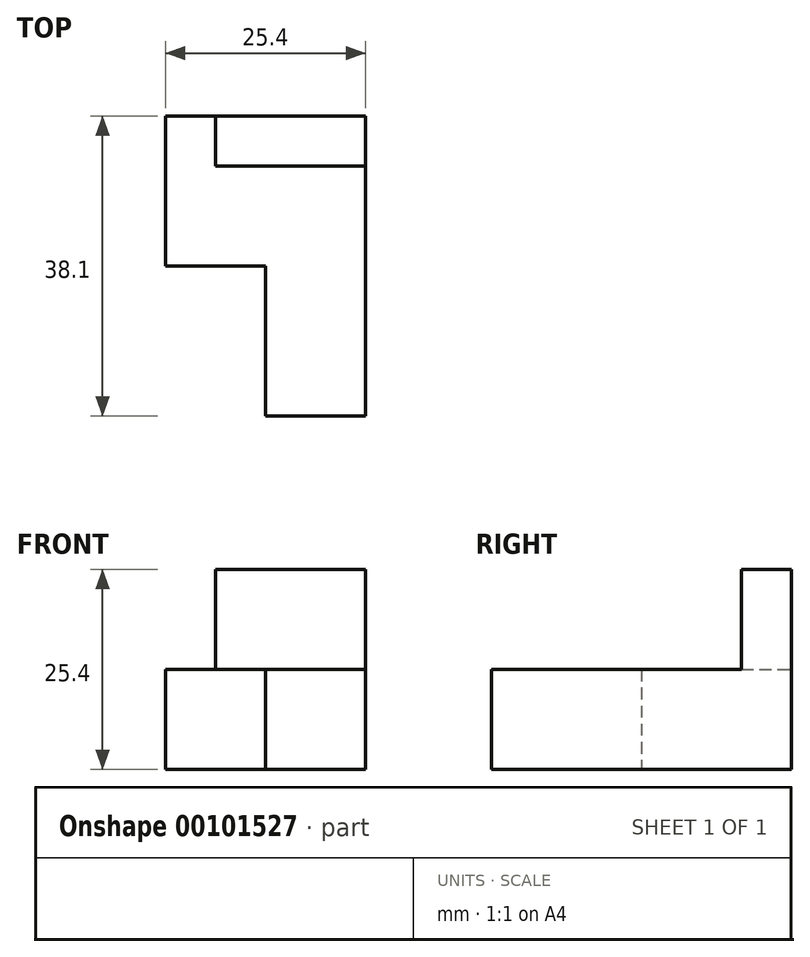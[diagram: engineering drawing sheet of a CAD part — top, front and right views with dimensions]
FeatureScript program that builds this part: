
annotation { "Feature Type Name" : "Feature", "Feature Type Description" : "" }
export const myFeature = defineFeature(function(context is Context, id is Id, definition is map)
    precondition{}
    {
        {
            var Q0;
            Q0=qCreatedBy(makeId("Front.planeOp"),FACE);
            var sketch = newSketch(context, id + "F0", { "sketchPlane" : qUnion([Q0])});
            skLineSegment(sketch, "E0", {"start": v(0, 0) * mm, "end": v(0, 12.7) * mm});
            skLineSegment(sketch, "E1", {"start": v(0, 12.7) * mm, "end": v(12.7, 12.7) * mm});
            skLineSegment(sketch, "E2", {"start": v(12.7, 12.7) * mm, "end": v(12.7, 0) * mm});
            skLineSegment(sketch, "E3", {"start": v(12.7, 0) * mm, "end": v(0, 0) * mm});
            skLineSegment(sketch, "E4", {"start": v(12.7, 12.7) * mm, "end": v(25.4, 12.7) * mm});
            skLineSegment(sketch, "E5", {"start": v(25.4, 12.7) * mm, "end": v(25.4, 0) * mm});
            skLineSegment(sketch, "E6", {"start": v(25.4, 0) * mm, "end": v(12.7, 0) * mm});
            skSolve(sketch);
        }
        {
            var Q0;
            Q0=makeQuery(id+"F0.imprint","IMPRINT",FACE,{"disambiguationData":[TD([[makeQuery(id+"F0.imprint","IMPRINT",EDGE,{"derivedFrom":sQuery(id+"F0.wireOp",EDGE,"E2")}),1.0]])]});
            extrude(context, id + "F1", {"entities" : qUnion([Q0]), "depth" : 38.1 * mm});
        }
        {
            var Q0;
            Q0=makeQuery(id+"F0.imprint","IMPRINT",FACE,{"disambiguationData":[TD([[makeQuery(id+"F0.imprint","IMPRINT",EDGE,{"derivedFrom":sQuery(id+"F0.wireOp",EDGE,"E0")}),-1.0]])]});
            extrude(context, id + "F2", {"entities" : qUnion([Q0]), "operationType" : NewBodyOperationType.ADD, "depth" : 19.05 * mm});
        }
        {
            var Q0;
            Q0=makeQuery(id+"F1.opExtrude","SWEPT_FACE",FACE,{"disambiguationData":[OSD([sQuery(id+"F0.wireOp",EDGE,"E5")])]});
            var sketch = newSketch(context, id + "F3", { "sketchPlane" : qUnion([Q0])});
            skLineSegment(sketch, "E7", {"start": v(0, 12.7) * mm, "end": v(0, 25.4) * mm});
            skLineSegment(sketch, "E8", {"start": v(0, 25.4) * mm, "end": v(-6.35, 25.4) * mm});
            skLineSegment(sketch, "E9", {"start": v(-6.35, 25.4) * mm, "end": v(-6.35, 12.7) * mm});
            skLineSegment(sketch, "E10", {"start": v(-6.35, 12.7) * mm, "end": v(0, 12.7) * mm});
            skSolve(sketch);
        }
        {
            var Q0;
            Q0=makeQuery(id+"F3.imprint","IMPRINT",FACE,{"disambiguationData":[TD([[makeQuery(id+"F3.imprint","IMPRINT",EDGE,{"derivedFrom":sQuery(id+"F3.wireOp",EDGE,"E7")}),1.0]])]});
            extrude(context, id + "F4", {"entities" : qUnion([Q0]), "operationType" : NewBodyOperationType.ADD, "oppositeDirection" : true, "depth" : 19.05 * mm});
        }
    });
